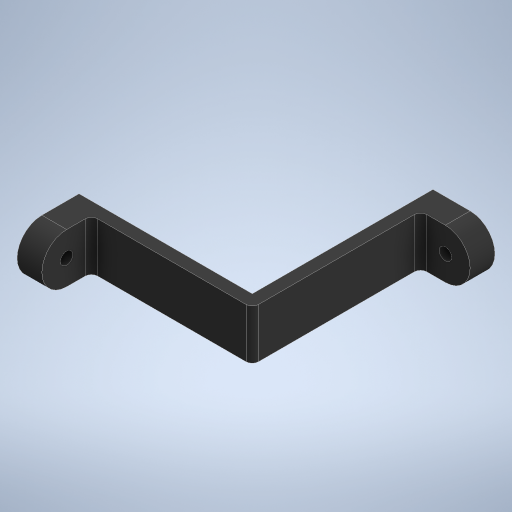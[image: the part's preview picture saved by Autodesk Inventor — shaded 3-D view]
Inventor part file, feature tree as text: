
AUTODESK INVENTOR PART (.ipt)
format: ipt  version: 2024 (Build 280153000, 153)  size: 312,832 bytes
history: native  units: in
note: dims shown in document units (in); Inventor stores cm internally (conversion verified against a paired STEP export)
features: extrude x5, sketch x5, fillet x4, projected_geometry x2
ambient origin geometry x8: Origin, YZ Plane, XZ Plane, XY Plane, X Axis, Y Axis, Z Axis, Center Point
bodies: Solid1 (feature_tree)
feature tree (16):
  extrude  "Extrusion1"  Depth=0.5in
  fillet  "Fillet1"  Radius=0.25in
  fillet  "Fillet2"  Radius=0.5in
  extrude  "Extrusion2"  Depth=0.5in
  extrude  "Extrusion3"  Depth=1.0in TaperAngle=0.0deg
  extrude  "Extrusion4"  Depth=0.5in
  fillet  "Fillet3"  Radius=0.25in
  fillet  "Fillet4"  Radius=0.25in
  extrude  "Extrusion5"  Depth=0.5in
  sketch  "Sketch1"  dims[d0=3.4in d1=7.1in d2=0.25in d3=0.5in]
  sketch  "Sketch2"  dims[d4=1.0in d5=0.5in]
  projected_geometry  "Projected Loop1"
  projected_geometry  "Projected Loop2"
  sketch  "Sketch3"  dims[d6=1.0in d7=1.0in d8=0.0in]
  sketch  "Sketch4"  dims[d9=0.125in d10=0.5in d11=0.25in d12=0.25in]
  sketch  "Sketch5"  dims[d13=1.0in d14=0.0in d15=0.5in d16=1.0in d17=0.0in d18=0.0in d19=0.0in d20=0.5in d21=0.125in d22=0.25in d23=1.0in d24=0.0in]
